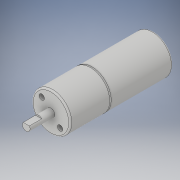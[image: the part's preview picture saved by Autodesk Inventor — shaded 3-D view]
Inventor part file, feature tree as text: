
AUTODESK INVENTOR PART (.ipt)
format: ipt  version: 2019 (Build 230136000, 136)  size: 148,992 bytes
history: native  units: mm
features: extrude x5, sketch x5, fillet x2, projected_geometry x1
ambient origin geometry x8: Origin, YZ Plane, XZ Plane, XY Plane, X Axis, Y Axis, Z Axis, Center Point
bodies: Solid1 (feature_tree)
feature tree (13):
  extrude  "Extrusion1"  Depth=26.5mm TaperAngle=0.0deg
  fillet  "Fillet1"  Radius=1.0mm
  extrude  "Extrusion2"  Depth=3.5mm
  extrude  "Extrusion3"  Depth=10.0mm TaperAngle=0.0deg
  extrude  "Extrusion4"  Depth=40.0mm TaperAngle=0.0deg
  extrude  "Extrusion5"  Depth=16.0mm TaperAngle=0.0deg
  fillet  "Fillet2"  Radius=8.0mm
  sketch  "Sketch1"  dims[d0=25.0mm d1=26.5mm d2=0.0mm d3=1.0mm]
  sketch  "Sketch2"  dims[d5=3.5mm d6=3.5mm]
  sketch  "Sketch3"  dims[d7=16.5mm d8=10.0mm d9=0.0mm]
  sketch  "Sketch4"  dims[d10=24.9mm d11=40.0mm d12=0.0mm]
  sketch  "Sketch5"  dims[d13=5.0mm d14=16.0mm d15=0.0mm d16=8.0mm d17=0.0mm d18=1.0mm]
  projected_geometry  "Projected Loop1"
